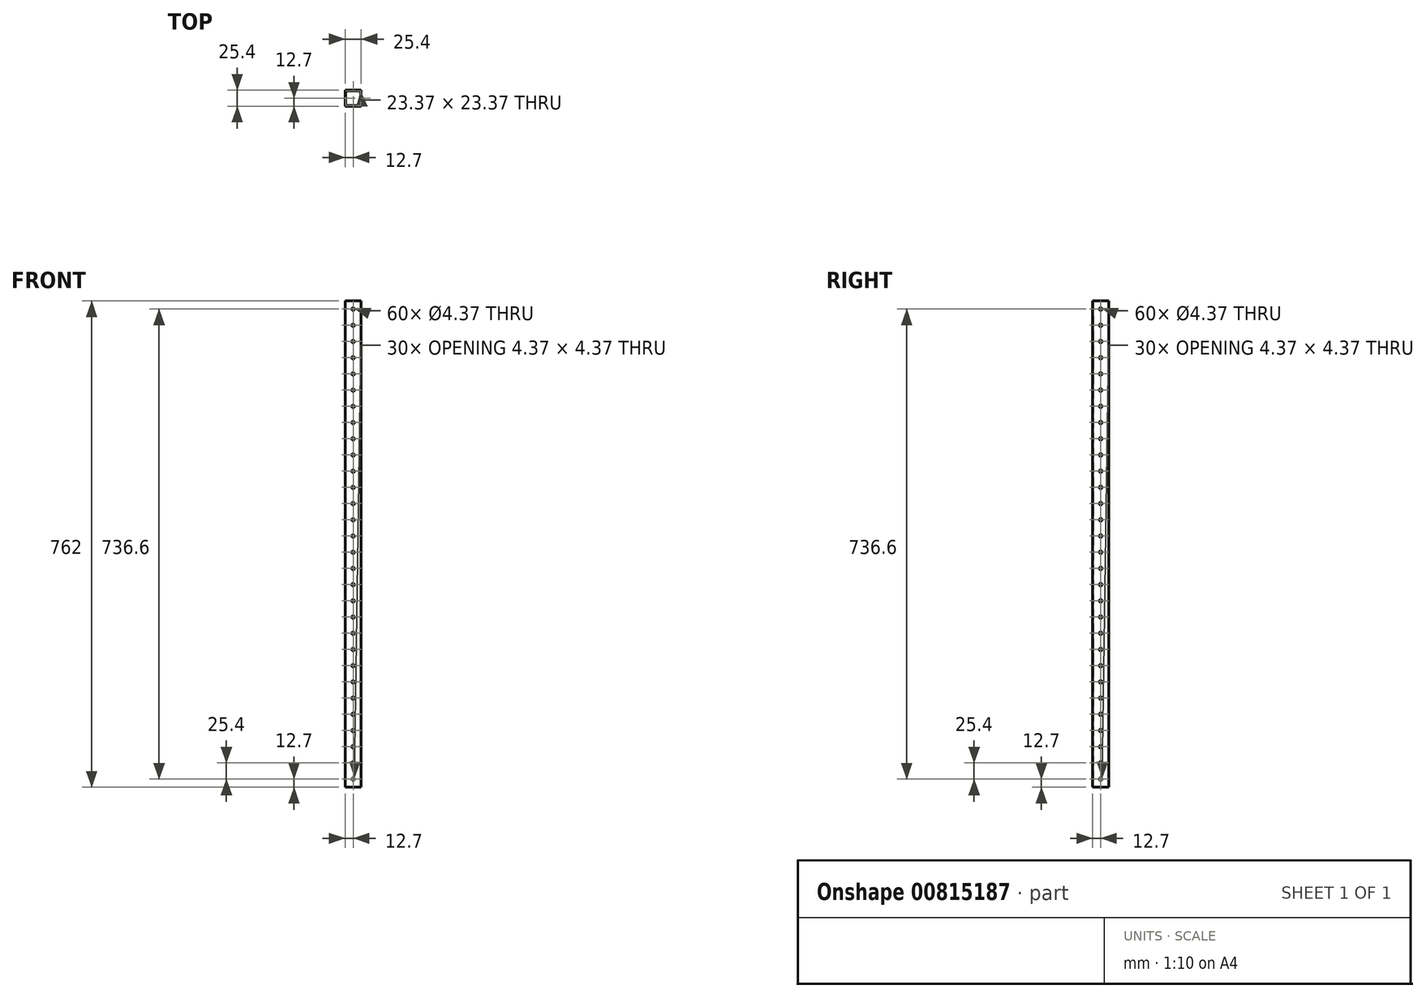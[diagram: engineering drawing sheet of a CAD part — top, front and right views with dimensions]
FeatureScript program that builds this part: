
annotation { "Feature Type Name" : "Feature", "Feature Type Description" : "" }
export const myFeature = defineFeature(function(context is Context, id is Id, definition is map)
    precondition{}
    {
        {
            var Q0;
            Q0=qCreatedBy(makeId("Top.planeOp"),FACE);
            var sketch = newSketch(context, id + "F0", { "sketchPlane" : qUnion([Q0])});
            skLineSegment(sketch, "E0.bottom", {"start": v(0, 0) * mm, "end": v(25.4, 0) * mm});
            skLineSegment(sketch, "E0.top", {"start": v(0, -25.4) * mm, "end": v(25.4, -25.4) * mm});
            skLineSegment(sketch, "E0.left", {"start": v(0, 0) * mm, "end": v(0, -25.4) * mm});
            skLineSegment(sketch, "E0.right", {"start": v(25.4, 0) * mm, "end": v(25.4, -25.4) * mm});
            skLineSegment(sketch, "E1.bottom", {"start": v(1.02, -1.02) * mm, "end": v(24.38, -1.02) * mm});
            skLineSegment(sketch, "E1.top", {"start": v(1.02, -24.38) * mm, "end": v(24.38, -24.38) * mm});
            skLineSegment(sketch, "E1.left", {"start": v(1.02, -1.02) * mm, "end": v(1.02, -24.38) * mm});
            skLineSegment(sketch, "E1.right", {"start": v(24.38, -1.02) * mm, "end": v(24.38, -24.38) * mm});
            skSolve(sketch);
        }
        {
            var Q0;
            Q0=makeQuery(id+"F0.imprint","IMPRINT",FACE,{"disambiguationData":[TD([[makeQuery(id+"F0.imprint","IMPRINT",EDGE,{"derivedFrom":sQuery(id+"F0.wireOp",EDGE,"E0.bottom")}),-1.0]])]});
            extrude(context, id + "F1", {"entities" : qUnion([Q0]), "depth" : 762 * mm, "offsetDistance" : 25.4 * mm});
        }
        {
            var Q0;
            Q0=makeQuery(id+"F1.opExtrude","SWEPT_FACE",FACE,{"disambiguationData":[OSD([sQuery(id+"F0.wireOp",EDGE,"E0.top")])]});
            var sketch = newSketch(context, id + "F2", { "sketchPlane" : qUnion([Q0])});
            skCircle(sketch, "E2", {"center": v(12.7, 12.7) * mm, "radius": 2.18 * mm});
            skCircle(sketch, "E3.0.1.0", {"center": v(12.7, 38.1) * mm, "radius": 2.18 * mm});
            skCircle(sketch, "E3.0.2.0", {"center": v(12.7, 63.5) * mm, "radius": 2.18 * mm});
            skCircle(sketch, "E3.0.3.0", {"center": v(12.7, 88.9) * mm, "radius": 2.18 * mm});
            skCircle(sketch, "E3.0.4.0", {"center": v(12.7, 114.3) * mm, "radius": 2.18 * mm});
            skCircle(sketch, "E3.0.5.0", {"center": v(12.7, 139.7) * mm, "radius": 2.18 * mm});
            skCircle(sketch, "E3.0.6.0", {"center": v(12.7, 165.1) * mm, "radius": 2.18 * mm});
            skCircle(sketch, "E3.0.7.0", {"center": v(12.7, 190.5) * mm, "radius": 2.18 * mm});
            skCircle(sketch, "E3.0.8.0", {"center": v(12.7, 215.9) * mm, "radius": 2.18 * mm});
            skCircle(sketch, "E3.0.9.0", {"center": v(12.7, 241.3) * mm, "radius": 2.18 * mm});
            skCircle(sketch, "E3.0.10.0", {"center": v(12.7, 266.7) * mm, "radius": 2.18 * mm});
            skCircle(sketch, "E3.0.11.0", {"center": v(12.7, 292.1) * mm, "radius": 2.18 * mm});
            skCircle(sketch, "E3.0.12.0", {"center": v(12.7, 317.5) * mm, "radius": 2.18 * mm});
            skCircle(sketch, "E3.0.13.0", {"center": v(12.7, 342.9) * mm, "radius": 2.18 * mm});
            skCircle(sketch, "E3.0.14.0", {"center": v(12.7, 368.3) * mm, "radius": 2.18 * mm});
            skCircle(sketch, "E3.0.15.0", {"center": v(12.7, 393.7) * mm, "radius": 2.18 * mm});
            skCircle(sketch, "E3.0.16.0", {"center": v(12.7, 419.1) * mm, "radius": 2.18 * mm});
            skCircle(sketch, "E3.0.17.0", {"center": v(12.7, 444.5) * mm, "radius": 2.18 * mm});
            skCircle(sketch, "E3.0.18.0", {"center": v(12.7, 469.9) * mm, "radius": 2.18 * mm});
            skCircle(sketch, "E3.0.19.0", {"center": v(12.7, 495.3) * mm, "radius": 2.18 * mm});
            skCircle(sketch, "E3.0.20.0", {"center": v(12.7, 520.7) * mm, "radius": 2.18 * mm});
            skCircle(sketch, "E3.0.21.0", {"center": v(12.7, 546.1) * mm, "radius": 2.18 * mm});
            skCircle(sketch, "E3.0.22.0", {"center": v(12.7, 571.5) * mm, "radius": 2.18 * mm});
            skCircle(sketch, "E3.0.23.0", {"center": v(12.7, 596.9) * mm, "radius": 2.18 * mm});
            skCircle(sketch, "E3.0.24.0", {"center": v(12.7, 622.3) * mm, "radius": 2.18 * mm});
            skLineSegment(sketch, "E3.direction1", {"start": v(12.7, 12.7) * mm, "end": v(38.1, 12.7) * mm, "construction": true});
            skLineSegment(sketch, "E3.direction2", {"start": v(12.7, 12.7) * mm, "end": v(12.7, 38.1) * mm, "construction": true});
            skCircle(sketch, "E4.0.0.25", {"center": v(12.7, 647.7) * mm, "radius": 2.18 * mm});
            skCircle(sketch, "E4.0.0.26", {"center": v(12.7, 673.1) * mm, "radius": 2.18 * mm});
            skCircle(sketch, "E4.0.0.27", {"center": v(12.7, 698.5) * mm, "radius": 2.18 * mm});
            skCircle(sketch, "E4.0.0.28", {"center": v(12.7, 723.9) * mm, "radius": 2.18 * mm});
            skCircle(sketch, "E5.0.0.29", {"center": v(12.7, 749.3) * mm, "radius": 2.18 * mm});
            skSolve(sketch);
        }
        {
            var Q0;
            Q0=makeQuery(id+"F2.imprint","IMPRINT",FACE,{"disambiguationData":[TD([[makeQuery(id+"F2.imprint","IMPRINT",EDGE,{"derivedFrom":sQuery(id+"F2.wireOp",EDGE,"E2")}),1.0]])]});
            var Q1;
            Q1=makeQuery(id+"F2.imprint","IMPRINT",FACE,{"disambiguationData":[TD([[makeQuery(id+"F2.imprint","IMPRINT",EDGE,{"derivedFrom":sQuery(id+"F2.wireOp",EDGE,"E3.0.1.0")}),1.0]])]});
            var Q2;
            Q2=makeQuery(id+"F2.imprint","IMPRINT",FACE,{"disambiguationData":[TD([[makeQuery(id+"F2.imprint","IMPRINT",EDGE,{"derivedFrom":sQuery(id+"F2.wireOp",EDGE,"E3.0.9.0")}),1.0]])]});
            var Q3;
            Q3=makeQuery(id+"F2.imprint","IMPRINT",FACE,{"disambiguationData":[TD([[makeQuery(id+"F2.imprint","IMPRINT",EDGE,{"derivedFrom":sQuery(id+"F2.wireOp",EDGE,"E3.0.8.0")}),1.0]])]});
            var Q4;
            Q4=makeQuery(id+"F2.imprint","IMPRINT",FACE,{"disambiguationData":[TD([[makeQuery(id+"F2.imprint","IMPRINT",EDGE,{"derivedFrom":sQuery(id+"F2.wireOp",EDGE,"E3.0.7.0")}),1.0]])]});
            var Q5;
            Q5=makeQuery(id+"F2.imprint","IMPRINT",FACE,{"disambiguationData":[TD([[makeQuery(id+"F2.imprint","IMPRINT",EDGE,{"derivedFrom":sQuery(id+"F2.wireOp",EDGE,"E3.0.6.0")}),1.0]])]});
            var Q6;
            Q6=makeQuery(id+"F2.imprint","IMPRINT",FACE,{"disambiguationData":[TD([[makeQuery(id+"F2.imprint","IMPRINT",EDGE,{"derivedFrom":sQuery(id+"F2.wireOp",EDGE,"E3.0.5.0")}),1.0]])]});
            var Q7;
            Q7=makeQuery(id+"F2.imprint","IMPRINT",FACE,{"disambiguationData":[TD([[makeQuery(id+"F2.imprint","IMPRINT",EDGE,{"derivedFrom":sQuery(id+"F2.wireOp",EDGE,"E3.0.4.0")}),1.0]])]});
            var Q8;
            Q8=makeQuery(id+"F2.imprint","IMPRINT",FACE,{"disambiguationData":[TD([[makeQuery(id+"F2.imprint","IMPRINT",EDGE,{"derivedFrom":sQuery(id+"F2.wireOp",EDGE,"E3.0.3.0")}),1.0]])]});
            var Q9;
            Q9=makeQuery(id+"F2.imprint","IMPRINT",FACE,{"disambiguationData":[TD([[makeQuery(id+"F2.imprint","IMPRINT",EDGE,{"derivedFrom":sQuery(id+"F2.wireOp",EDGE,"E3.0.2.0")}),1.0]])]});
            var Q10;
            Q10=makeQuery(id+"F2.imprint","IMPRINT",FACE,{"disambiguationData":[TD([[makeQuery(id+"F2.imprint","IMPRINT",EDGE,{"derivedFrom":sQuery(id+"F2.wireOp",EDGE,"E3.0.10.0")}),1.0]])]});
            var Q11;
            Q11=makeQuery(id+"F2.imprint","IMPRINT",FACE,{"disambiguationData":[TD([[makeQuery(id+"F2.imprint","IMPRINT",EDGE,{"derivedFrom":sQuery(id+"F2.wireOp",EDGE,"E3.0.11.0")}),1.0]])]});
            var Q12;
            Q12=makeQuery(id+"F2.imprint","IMPRINT",FACE,{"disambiguationData":[TD([[makeQuery(id+"F2.imprint","IMPRINT",EDGE,{"derivedFrom":sQuery(id+"F2.wireOp",EDGE,"E3.0.12.0")}),1.0]])]});
            var Q13;
            Q13=makeQuery(id+"F2.imprint","IMPRINT",FACE,{"disambiguationData":[TD([[makeQuery(id+"F2.imprint","IMPRINT",EDGE,{"derivedFrom":sQuery(id+"F2.wireOp",EDGE,"E3.0.13.0")}),1.0]])]});
            var Q14;
            Q14=makeQuery(id+"F2.imprint","IMPRINT",FACE,{"disambiguationData":[TD([[makeQuery(id+"F2.imprint","IMPRINT",EDGE,{"derivedFrom":sQuery(id+"F2.wireOp",EDGE,"E3.0.14.0")}),1.0]])]});
            var Q15;
            Q15=makeQuery(id+"F2.imprint","IMPRINT",FACE,{"disambiguationData":[TD([[makeQuery(id+"F2.imprint","IMPRINT",EDGE,{"derivedFrom":sQuery(id+"F2.wireOp",EDGE,"E3.0.15.0")}),1.0]])]});
            var Q16;
            Q16=makeQuery(id+"F2.imprint","IMPRINT",FACE,{"disambiguationData":[TD([[makeQuery(id+"F2.imprint","IMPRINT",EDGE,{"derivedFrom":sQuery(id+"F2.wireOp",EDGE,"E3.0.16.0")}),1.0]])]});
            var Q17;
            Q17=makeQuery(id+"F2.imprint","IMPRINT",FACE,{"disambiguationData":[TD([[makeQuery(id+"F2.imprint","IMPRINT",EDGE,{"derivedFrom":sQuery(id+"F2.wireOp",EDGE,"E3.0.17.0")}),1.0]])]});
            var Q18;
            Q18=makeQuery(id+"F2.imprint","IMPRINT",FACE,{"disambiguationData":[TD([[makeQuery(id+"F2.imprint","IMPRINT",EDGE,{"derivedFrom":sQuery(id+"F2.wireOp",EDGE,"E3.0.18.0")}),1.0]])]});
            var Q19;
            Q19=makeQuery(id+"F2.imprint","IMPRINT",FACE,{"disambiguationData":[TD([[makeQuery(id+"F2.imprint","IMPRINT",EDGE,{"derivedFrom":sQuery(id+"F2.wireOp",EDGE,"E3.0.19.0")}),1.0]])]});
            var Q20;
            Q20=makeQuery(id+"F2.imprint","IMPRINT",FACE,{"disambiguationData":[TD([[makeQuery(id+"F2.imprint","IMPRINT",EDGE,{"derivedFrom":sQuery(id+"F2.wireOp",EDGE,"E3.0.20.0")}),1.0]])]});
            var Q21;
            Q21=makeQuery(id+"F2.imprint","IMPRINT",FACE,{"disambiguationData":[TD([[makeQuery(id+"F2.imprint","IMPRINT",EDGE,{"derivedFrom":sQuery(id+"F2.wireOp",EDGE,"E3.0.21.0")}),1.0]])]});
            var Q22;
            Q22=makeQuery(id+"F2.imprint","IMPRINT",FACE,{"disambiguationData":[TD([[makeQuery(id+"F2.imprint","IMPRINT",EDGE,{"derivedFrom":sQuery(id+"F2.wireOp",EDGE,"E3.0.22.0")}),1.0]])]});
            var Q23;
            Q23=makeQuery(id+"F2.imprint","IMPRINT",FACE,{"disambiguationData":[TD([[makeQuery(id+"F2.imprint","IMPRINT",EDGE,{"derivedFrom":sQuery(id+"F2.wireOp",EDGE,"E3.0.23.0")}),1.0]])]});
            var Q24;
            Q24=makeQuery(id+"F2.imprint","IMPRINT",FACE,{"disambiguationData":[TD([[makeQuery(id+"F2.imprint","IMPRINT",EDGE,{"derivedFrom":sQuery(id+"F2.wireOp",EDGE,"E3.0.24.0")}),1.0]])]});
            var Q25;
            Q25=makeQuery(id+"F2.imprint","IMPRINT",FACE,{"disambiguationData":[TD([[makeQuery(id+"F2.imprint","IMPRINT",EDGE,{"derivedFrom":sQuery(id+"F2.wireOp",EDGE,"E4.0.0.25")}),1.0]])]});
            var Q26;
            Q26=makeQuery(id+"F2.imprint","IMPRINT",FACE,{"disambiguationData":[TD([[makeQuery(id+"F2.imprint","IMPRINT",EDGE,{"derivedFrom":sQuery(id+"F2.wireOp",EDGE,"E4.0.0.26")}),1.0]])]});
            var Q27;
            Q27=makeQuery(id+"F2.imprint","IMPRINT",FACE,{"disambiguationData":[TD([[makeQuery(id+"F2.imprint","IMPRINT",EDGE,{"derivedFrom":sQuery(id+"F2.wireOp",EDGE,"E4.0.0.27")}),1.0]])]});
            var Q28;
            Q28=makeQuery(id+"F2.imprint","IMPRINT",FACE,{"disambiguationData":[TD([[makeQuery(id+"F2.imprint","IMPRINT",EDGE,{"derivedFrom":sQuery(id+"F2.wireOp",EDGE,"E4.0.0.28")}),1.0]])]});
            var Q29;
            Q29=makeQuery(id+"F2.imprint","IMPRINT",FACE,{"disambiguationData":[TD([[makeQuery(id+"F2.imprint","IMPRINT",EDGE,{"derivedFrom":sQuery(id+"F2.wireOp",EDGE,"E5.0.0.29")}),1.0]])]});
            extrude(context, id + "F3", {"entities" : qUnion([Q0, Q1, Q2, Q3, Q4, Q5, Q6, Q7, Q8, Q9, Q10, Q11, Q12, Q13, Q14, Q15, Q16, Q17, Q18, Q19, Q20, Q21, Q22, Q23, Q24, Q25, Q26, Q27, Q28, Q29]), "operationType" : NewBodyOperationType.REMOVE, "oppositeDirection" : true, "depth" : 25.4 * mm, "offsetDistance" : 25.4 * mm});
        }
        {
            var Q0;
            Q0=makeQuery(id+"F1.opExtrude","SWEPT_FACE",FACE,{"disambiguationData":[OSD([sQuery(id+"F0.wireOp",EDGE,"E0.left")])]});
            var sketch = newSketch(context, id + "F4", { "sketchPlane" : qUnion([Q0])});
            skCircle(sketch, "E6", {"center": v(12.7, 12.7) * mm, "radius": 2.18 * mm});
            skCircle(sketch, "E7.0.1.0", {"center": v(12.7, 38.1) * mm, "radius": 2.18 * mm});
            skCircle(sketch, "E7.0.2.0", {"center": v(12.7, 63.5) * mm, "radius": 2.18 * mm});
            skCircle(sketch, "E7.0.3.0", {"center": v(12.7, 88.9) * mm, "radius": 2.18 * mm});
            skCircle(sketch, "E7.0.4.0", {"center": v(12.7, 114.3) * mm, "radius": 2.18 * mm});
            skCircle(sketch, "E7.0.5.0", {"center": v(12.7, 139.7) * mm, "radius": 2.18 * mm});
            skCircle(sketch, "E7.0.6.0", {"center": v(12.7, 165.1) * mm, "radius": 2.18 * mm});
            skCircle(sketch, "E7.0.7.0", {"center": v(12.7, 190.5) * mm, "radius": 2.18 * mm});
            skCircle(sketch, "E7.0.8.0", {"center": v(12.7, 215.9) * mm, "radius": 2.18 * mm});
            skCircle(sketch, "E7.0.9.0", {"center": v(12.7, 241.3) * mm, "radius": 2.18 * mm});
            skCircle(sketch, "E7.0.10.0", {"center": v(12.7, 266.7) * mm, "radius": 2.18 * mm});
            skCircle(sketch, "E7.0.11.0", {"center": v(12.7, 292.1) * mm, "radius": 2.18 * mm});
            skCircle(sketch, "E7.0.12.0", {"center": v(12.7, 317.5) * mm, "radius": 2.18 * mm});
            skCircle(sketch, "E7.0.13.0", {"center": v(12.7, 342.9) * mm, "radius": 2.18 * mm});
            skCircle(sketch, "E7.0.14.0", {"center": v(12.7, 368.3) * mm, "radius": 2.18 * mm});
            skCircle(sketch, "E7.0.15.0", {"center": v(12.7, 393.7) * mm, "radius": 2.18 * mm});
            skCircle(sketch, "E7.0.16.0", {"center": v(12.7, 419.1) * mm, "radius": 2.18 * mm});
            skCircle(sketch, "E7.0.17.0", {"center": v(12.7, 444.5) * mm, "radius": 2.18 * mm});
            skCircle(sketch, "E7.0.18.0", {"center": v(12.7, 469.9) * mm, "radius": 2.18 * mm});
            skCircle(sketch, "E7.0.19.0", {"center": v(12.7, 495.3) * mm, "radius": 2.18 * mm});
            skCircle(sketch, "E7.0.20.0", {"center": v(12.7, 520.7) * mm, "radius": 2.18 * mm});
            skCircle(sketch, "E7.0.21.0", {"center": v(12.7, 546.1) * mm, "radius": 2.18 * mm});
            skCircle(sketch, "E7.0.22.0", {"center": v(12.7, 571.5) * mm, "radius": 2.18 * mm});
            skCircle(sketch, "E7.0.23.0", {"center": v(12.7, 596.9) * mm, "radius": 2.18 * mm});
            skCircle(sketch, "E7.0.24.0", {"center": v(12.7, 622.3) * mm, "radius": 2.18 * mm});
            skLineSegment(sketch, "E7.direction1", {"start": v(12.7, 12.7) * mm, "end": v(38.1, 12.7) * mm, "construction": true});
            skLineSegment(sketch, "E7.direction2", {"start": v(12.7, 12.7) * mm, "end": v(12.7, 38.1) * mm, "construction": true});
            skCircle(sketch, "E8.0.0.25", {"center": v(12.7, 647.7) * mm, "radius": 2.18 * mm});
            skCircle(sketch, "E8.0.0.26", {"center": v(12.7, 673.1) * mm, "radius": 2.18 * mm});
            skCircle(sketch, "E8.0.0.27", {"center": v(12.7, 698.5) * mm, "radius": 2.18 * mm});
            skCircle(sketch, "E8.0.0.28", {"center": v(12.7, 723.9) * mm, "radius": 2.18 * mm});
            skCircle(sketch, "E8.0.0.29", {"center": v(12.7, 749.3) * mm, "radius": 2.18 * mm});
            skSolve(sketch);
        }
        {
            var Q0;
            Q0=makeQuery(id+"F4.imprint","IMPRINT",FACE,{"disambiguationData":[TD([[makeQuery(id+"F4.imprint","IMPRINT",EDGE,{"derivedFrom":sQuery(id+"F4.wireOp",EDGE,"E6")}),1.0]])]});
            var Q1;
            Q1=makeQuery(id+"F4.imprint","IMPRINT",FACE,{"disambiguationData":[TD([[makeQuery(id+"F4.imprint","IMPRINT",EDGE,{"derivedFrom":sQuery(id+"F4.wireOp",EDGE,"E7.0.1.0")}),1.0]])]});
            var Q2;
            Q2=makeQuery(id+"F4.imprint","IMPRINT",FACE,{"disambiguationData":[TD([[makeQuery(id+"F4.imprint","IMPRINT",EDGE,{"derivedFrom":sQuery(id+"F4.wireOp",EDGE,"E7.0.2.0")}),1.0]])]});
            var Q3;
            Q3=makeQuery(id+"F4.imprint","IMPRINT",FACE,{"disambiguationData":[TD([[makeQuery(id+"F4.imprint","IMPRINT",EDGE,{"derivedFrom":sQuery(id+"F4.wireOp",EDGE,"E7.0.3.0")}),1.0]])]});
            var Q4;
            Q4=makeQuery(id+"F4.imprint","IMPRINT",FACE,{"disambiguationData":[TD([[makeQuery(id+"F4.imprint","IMPRINT",EDGE,{"derivedFrom":sQuery(id+"F4.wireOp",EDGE,"E7.0.4.0")}),1.0]])]});
            var Q5;
            Q5=makeQuery(id+"F4.imprint","IMPRINT",FACE,{"disambiguationData":[TD([[makeQuery(id+"F4.imprint","IMPRINT",EDGE,{"derivedFrom":sQuery(id+"F4.wireOp",EDGE,"E7.0.5.0")}),1.0]])]});
            var Q6;
            Q6=makeQuery(id+"F4.imprint","IMPRINT",FACE,{"disambiguationData":[TD([[makeQuery(id+"F4.imprint","IMPRINT",EDGE,{"derivedFrom":sQuery(id+"F4.wireOp",EDGE,"E7.0.6.0")}),1.0]])]});
            var Q7;
            Q7=makeQuery(id+"F4.imprint","IMPRINT",FACE,{"disambiguationData":[TD([[makeQuery(id+"F4.imprint","IMPRINT",EDGE,{"derivedFrom":sQuery(id+"F4.wireOp",EDGE,"E7.0.7.0")}),1.0]])]});
            var Q8;
            Q8=makeQuery(id+"F4.imprint","IMPRINT",FACE,{"disambiguationData":[TD([[makeQuery(id+"F4.imprint","IMPRINT",EDGE,{"derivedFrom":sQuery(id+"F4.wireOp",EDGE,"E7.0.8.0")}),1.0]])]});
            var Q9;
            Q9=makeQuery(id+"F4.imprint","IMPRINT",FACE,{"disambiguationData":[TD([[makeQuery(id+"F4.imprint","IMPRINT",EDGE,{"derivedFrom":sQuery(id+"F4.wireOp",EDGE,"E7.0.9.0")}),1.0]])]});
            var Q10;
            Q10=makeQuery(id+"F4.imprint","IMPRINT",FACE,{"disambiguationData":[TD([[makeQuery(id+"F4.imprint","IMPRINT",EDGE,{"derivedFrom":sQuery(id+"F4.wireOp",EDGE,"E7.0.10.0")}),1.0]])]});
            var Q11;
            Q11=makeQuery(id+"F4.imprint","IMPRINT",FACE,{"disambiguationData":[TD([[makeQuery(id+"F4.imprint","IMPRINT",EDGE,{"derivedFrom":sQuery(id+"F4.wireOp",EDGE,"E7.0.11.0")}),1.0]])]});
            var Q12;
            Q12=makeQuery(id+"F4.imprint","IMPRINT",FACE,{"disambiguationData":[TD([[makeQuery(id+"F4.imprint","IMPRINT",EDGE,{"derivedFrom":sQuery(id+"F4.wireOp",EDGE,"E7.0.12.0")}),1.0]])]});
            var Q13;
            Q13=makeQuery(id+"F4.imprint","IMPRINT",FACE,{"disambiguationData":[TD([[makeQuery(id+"F4.imprint","IMPRINT",EDGE,{"derivedFrom":sQuery(id+"F4.wireOp",EDGE,"E7.0.13.0")}),1.0]])]});
            var Q14;
            Q14=makeQuery(id+"F4.imprint","IMPRINT",FACE,{"disambiguationData":[TD([[makeQuery(id+"F4.imprint","IMPRINT",EDGE,{"derivedFrom":sQuery(id+"F4.wireOp",EDGE,"E7.0.14.0")}),1.0]])]});
            var Q15;
            Q15=makeQuery(id+"F4.imprint","IMPRINT",FACE,{"disambiguationData":[TD([[makeQuery(id+"F4.imprint","IMPRINT",EDGE,{"derivedFrom":sQuery(id+"F4.wireOp",EDGE,"E7.0.15.0")}),1.0]])]});
            var Q16;
            Q16=makeQuery(id+"F4.imprint","IMPRINT",FACE,{"disambiguationData":[TD([[makeQuery(id+"F4.imprint","IMPRINT",EDGE,{"derivedFrom":sQuery(id+"F4.wireOp",EDGE,"E7.0.16.0")}),1.0]])]});
            var Q17;
            Q17=makeQuery(id+"F4.imprint","IMPRINT",FACE,{"disambiguationData":[TD([[makeQuery(id+"F4.imprint","IMPRINT",EDGE,{"derivedFrom":sQuery(id+"F4.wireOp",EDGE,"E7.0.17.0")}),1.0]])]});
            var Q18;
            Q18=makeQuery(id+"F4.imprint","IMPRINT",FACE,{"disambiguationData":[TD([[makeQuery(id+"F4.imprint","IMPRINT",EDGE,{"derivedFrom":sQuery(id+"F4.wireOp",EDGE,"E7.0.21.0")}),1.0]])]});
            var Q19;
            Q19=makeQuery(id+"F4.imprint","IMPRINT",FACE,{"disambiguationData":[TD([[makeQuery(id+"F4.imprint","IMPRINT",EDGE,{"derivedFrom":sQuery(id+"F4.wireOp",EDGE,"E7.0.20.0")}),1.0]])]});
            var Q20;
            Q20=makeQuery(id+"F4.imprint","IMPRINT",FACE,{"disambiguationData":[TD([[makeQuery(id+"F4.imprint","IMPRINT",EDGE,{"derivedFrom":sQuery(id+"F4.wireOp",EDGE,"E7.0.19.0")}),1.0]])]});
            var Q21;
            Q21=makeQuery(id+"F4.imprint","IMPRINT",FACE,{"disambiguationData":[TD([[makeQuery(id+"F4.imprint","IMPRINT",EDGE,{"derivedFrom":sQuery(id+"F4.wireOp",EDGE,"E7.0.18.0")}),1.0]])]});
            var Q22;
            Q22=makeQuery(id+"F4.imprint","IMPRINT",FACE,{"disambiguationData":[TD([[makeQuery(id+"F4.imprint","IMPRINT",EDGE,{"derivedFrom":sQuery(id+"F4.wireOp",EDGE,"E7.0.22.0")}),1.0]])]});
            var Q23;
            Q23=makeQuery(id+"F4.imprint","IMPRINT",FACE,{"disambiguationData":[TD([[makeQuery(id+"F4.imprint","IMPRINT",EDGE,{"derivedFrom":sQuery(id+"F4.wireOp",EDGE,"E7.0.23.0")}),1.0]])]});
            var Q24;
            Q24=makeQuery(id+"F4.imprint","IMPRINT",FACE,{"disambiguationData":[TD([[makeQuery(id+"F4.imprint","IMPRINT",EDGE,{"derivedFrom":sQuery(id+"F4.wireOp",EDGE,"E7.0.24.0")}),1.0]])]});
            var Q25;
            Q25=makeQuery(id+"F4.imprint","IMPRINT",FACE,{"disambiguationData":[TD([[makeQuery(id+"F4.imprint","IMPRINT",EDGE,{"derivedFrom":sQuery(id+"F4.wireOp",EDGE,"E8.0.0.25")}),1.0]])]});
            var Q26;
            Q26=makeQuery(id+"F4.imprint","IMPRINT",FACE,{"disambiguationData":[TD([[makeQuery(id+"F4.imprint","IMPRINT",EDGE,{"derivedFrom":sQuery(id+"F4.wireOp",EDGE,"E8.0.0.26")}),1.0]])]});
            var Q27;
            Q27=makeQuery(id+"F4.imprint","IMPRINT",FACE,{"disambiguationData":[TD([[makeQuery(id+"F4.imprint","IMPRINT",EDGE,{"derivedFrom":sQuery(id+"F4.wireOp",EDGE,"E8.0.0.27")}),1.0]])]});
            var Q28;
            Q28=makeQuery(id+"F4.imprint","IMPRINT",FACE,{"disambiguationData":[TD([[makeQuery(id+"F4.imprint","IMPRINT",EDGE,{"derivedFrom":sQuery(id+"F4.wireOp",EDGE,"E8.0.0.28")}),1.0]])]});
            var Q29;
            Q29=makeQuery(id+"F4.imprint","IMPRINT",FACE,{"disambiguationData":[TD([[makeQuery(id+"F4.imprint","IMPRINT",EDGE,{"derivedFrom":sQuery(id+"F4.wireOp",EDGE,"E8.0.0.29")}),1.0]])]});
            extrude(context, id + "F5", {"entities" : qUnion([Q0, Q1, Q2, Q3, Q4, Q5, Q6, Q7, Q8, Q9, Q10, Q11, Q12, Q13, Q14, Q15, Q16, Q17, Q18, Q19, Q20, Q21, Q22, Q23, Q24, Q25, Q26, Q27, Q28, Q29]), "operationType" : NewBodyOperationType.REMOVE, "oppositeDirection" : true, "depth" : 25.4 * mm, "offsetDistance" : 25.4 * mm});
        }
    });
